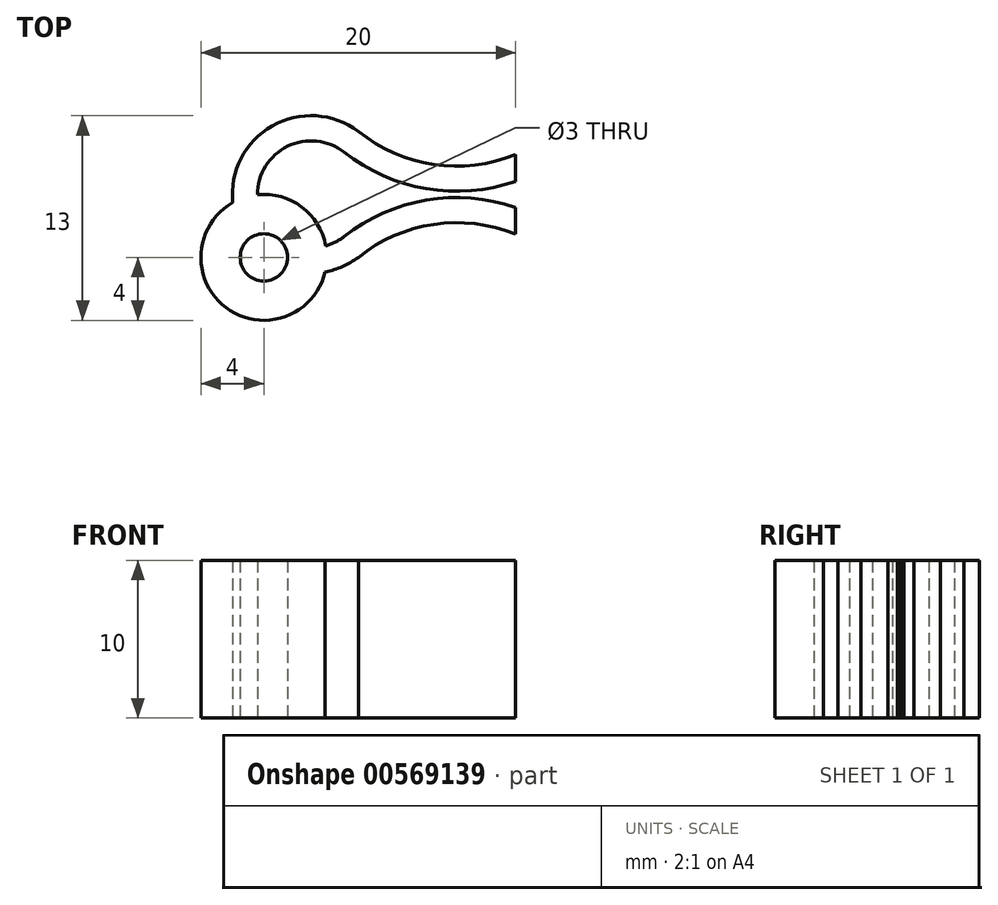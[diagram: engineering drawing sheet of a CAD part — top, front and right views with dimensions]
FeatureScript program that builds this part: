
annotation { "Feature Type Name" : "Feature", "Feature Type Description" : "" }
export const myFeature = defineFeature(function(context is Context, id is Id, definition is map)
    precondition{}
    {
        {
            var Q0;
            Q0=qCreatedBy(makeId("Top.planeOp"),FACE);
            var sketch = newSketch(context, id + "F0", { "sketchPlane" : qUnion([Q0])});
            skLineSegment(sketch, "E0", {"start": v(-5, 0) * mm, "end": v(13, 0) * mm, "construction": true});
            skArc(sketch, "E1", {"start": v(3, 4) * mm, "mid": v(7.8, 1.9) * mm, "end": v(13, 2.53) * mm});
            skLineSegment(sketch, "E2", {"start": v(-4.66, 1.8) * mm, "end": v(13, 1.8) * mm, "construction": true});
            skArc(sketch, "E3", {"start": v(2.1, 2.68) * mm, "mid": v(7.32, 0.37) * mm, "end": v(13, 0.82) * mm});
            skArc(sketch, "E4", {"start": v(2.1, 2.68) * mm, "mid": v(-1.49, 3.06) * mm, "end": v(-3.4, 0) * mm});
            skLineSegment(sketch, "E5", {"start": v(13, 2.53) * mm, "end": v(13, 0) * mm, "construction": true});
            skArc(sketch, "E6.trimOffspring", {"start": v(3, 4) * mm, "mid": v(-2.24, 4.47) * mm, "end": v(-5, 0) * mm});
            skLineSegment(sketch, "E7", {"start": v(13, 0.82) * mm, "end": v(13, 2.53) * mm});
            skArc(sketch, "E8.MirrorCS", {"start": v(2.1, -2.68) * mm, "mid": v(7.32, -0.37) * mm, "end": v(13, -0.82) * mm});
            skArc(sketch, "E9.MirrorCS", {"start": v(2.1, -2.68) * mm, "mid": v(1.55, -3.03) * mm, "end": v(0.93, -3.27) * mm});
            skArc(sketch, "E10.MirrorCS", {"start": v(3, -4) * mm, "mid": v(2, -4.58) * mm, "end": v(0.9, -4.92) * mm});
            skLineSegment(sketch, "E11.MirrorCS", {"start": v(13, -0.82) * mm, "end": v(13, -2.53) * mm});
            skArc(sketch, "E12.MirrorCS", {"start": v(3, -4) * mm, "mid": v(7.8, -1.9) * mm, "end": v(13, -2.53) * mm});
            skArc(sketch, "E13", {"start": v(0.93, -3.27) * mm, "mid": v(-0.6, -0.8) * mm, "end": v(-3.4, -0.02) * mm});
            skArc(sketch, "E14.trimOffspring", {"start": v(-3.4, -0.02) * mm, "mid": v(-3.4, -0.01) * mm, "end": v(-3.4, 0) * mm});
            skArc(sketch, "E15.trimOffspring", {"start": v(-4.97, -0.52) * mm, "mid": v(-5, -0.26) * mm, "end": v(-5, 0) * mm});
            skArc(sketch, "E16.trimOffspring", {"start": v(-4.97, -0.52) * mm, "mid": v(-5.4, -7.2) * mm, "end": v(0.9, -4.92) * mm});
            skCircle(sketch, "E17", {"center": v(-3, -4) * mm, "radius": 1.5 * mm});
            skSolve(sketch);
        }
        {
            var Q0;
            Q0=makeQuery(id+"F0.imprint","IMPRINT",FACE,{"disambiguationData":[TD([[makeQuery(id+"F0.imprint","IMPRINT",EDGE,{"derivedFrom":sQuery(id+"F0.wireOp",EDGE,"E1")}),-1.0]])]});
            extrude(context, id + "F1", {"entities" : qUnion([Q0]), "depth" : 10 * mm});
        }
    });
